# Revit family: 402_VCF-B-_-V-ZP-0-0
name_source: partatom
category: Mechanical Equipment
revit_build: Autodesk Revit 2018 (Build: 20170223_1515(x64)
units: mm (PartAtom-declared; Revit-internal decimal feet)

## family parameters
Always vertical = Yes
Cut with Voids When Loaded = No
Part Type = Normal
Room Calculation Point = No
Round Connector Dimension = Use Diameter
Shared = No
Work Plane-Based = No

## types (4) — shared parameters
CAT0 = Yes
Description = Air curtain FINESSE B, water heater
H2 = 299 mm  [stored 0.980971 ft]
H2__ve = -299 mm  [stored -0.980971 ft]
H3 = 2 mm  [stored 0.00656168 ft]
H3__ve = -2 mm  [stored -0.00656168 ft]
Manufacturer = 2VV
QmdConnectorList = 331;PHS;361;PHR
URL = www.2vv.cz
W3 = 298 mm  [stored 0.97769 ft]
W5 = 319 mm  [stored 1.04659 ft]
W6 = 119 mm
W7 = 179 mm
W8 = 89 mm
magiPartTypeId = 402
magiProductFamilyId = VCF-B-*-V-ZP-0-0

## per-type parameters (varying)
| type | A1 | B1 | L4 |
| VCF-B-100-V-ZP-0-0 | 528 mm | 562 mm  [stored 1.84383 ft] | 583 mm  [stored 1.91273 ft] |
| VCF-B-250-V-ZP-0-0 | 1218 mm | 1252 mm | 1273 mm |
| VCF-B-200-V-ZP-0-0 | 1028 mm | 1062 mm | 1083 mm |
| VCF-B-150-V-ZP-0-0 | 778 mm | 812 mm | 833 mm |

note: column(s) folded — value = type name in every type: MC Product Code, magiProductId

note: [stored X ft] marks values corroborated as IEEE doubles in the binary element streams (Revit-internal decimal feet)

## geometry (parser evidence)
native form markers: Blend x2, Sweep x3
no freeform markers — native parametric forms only
